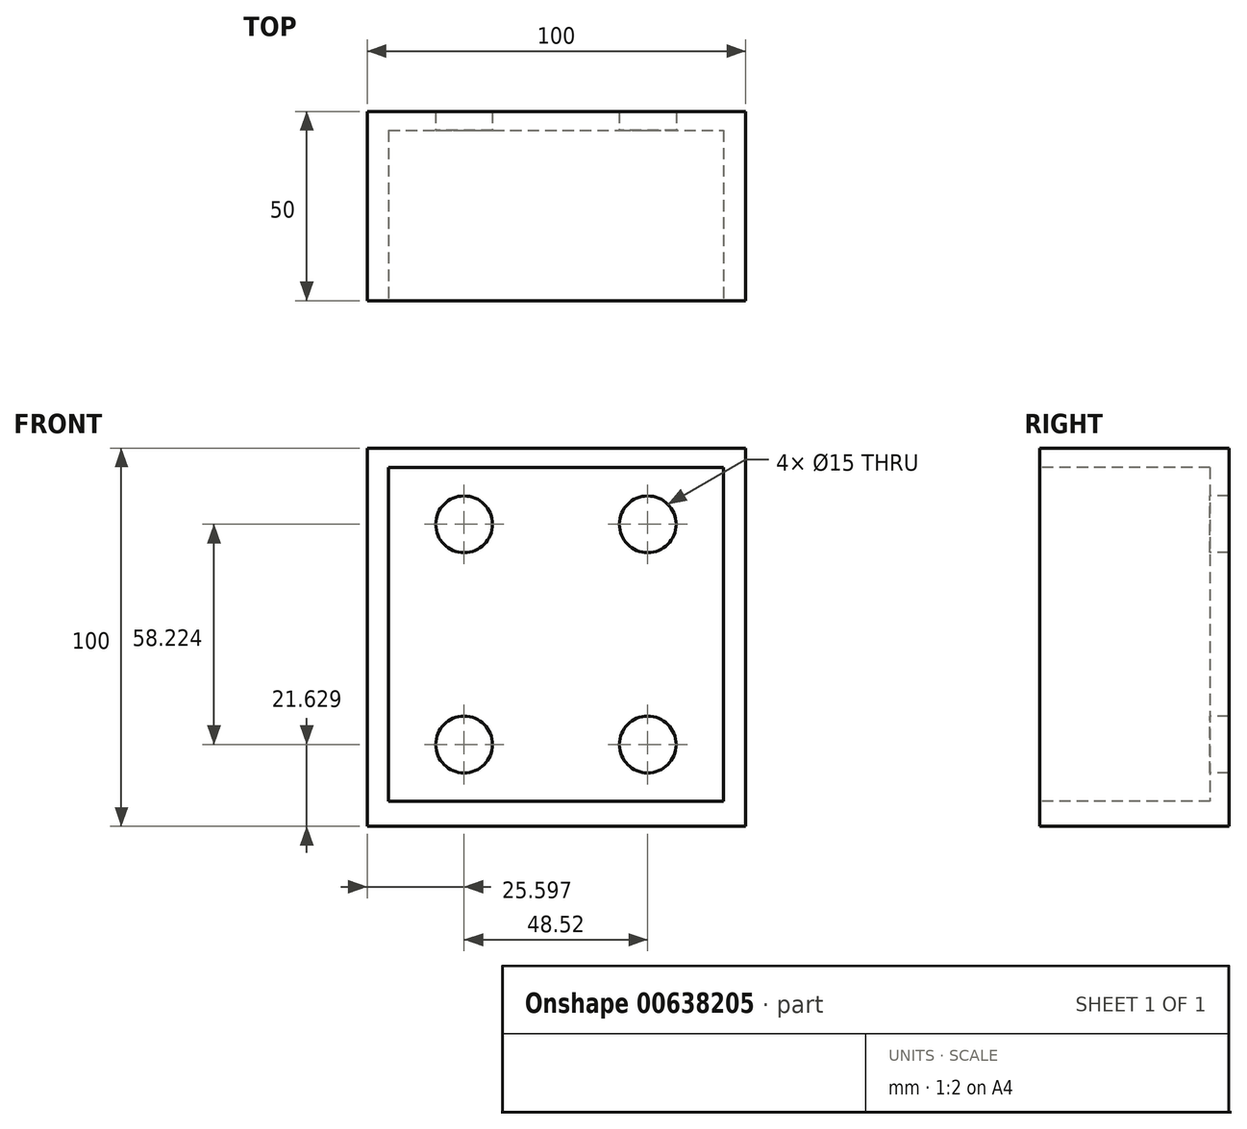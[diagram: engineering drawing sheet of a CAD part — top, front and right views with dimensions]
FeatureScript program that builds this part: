
annotation { "Feature Type Name" : "Feature", "Feature Type Description" : "" }
export const myFeature = defineFeature(function(context is Context, id is Id, definition is map)
    precondition{}
    {
        {
            var Q0;
            Q0=qCreatedBy(makeId("Front.planeOp"),FACE);
            var sketch = newSketch(context, id + "F0", { "sketchPlane" : qUnion([Q0])});
            skLineSegment(sketch, "E0.bottom", {"start": v(-46.6, 44.67) * mm, "end": v(53.4, 44.67) * mm});
            skLineSegment(sketch, "E0.top", {"start": v(-46.6, -55.33) * mm, "end": v(53.4, -55.33) * mm});
            skLineSegment(sketch, "E0.left", {"start": v(-46.6, 44.67) * mm, "end": v(-46.6, -55.33) * mm});
            skLineSegment(sketch, "E0.right", {"start": v(53.4, 44.67) * mm, "end": v(53.4, -55.33) * mm});
            skSolve(sketch);
        }
        {
            var Q0;
            Q0=makeQuery(id+"F0.imprint","IMPRINT",FACE,{"disambiguationData":[TD([[makeQuery(id+"F0.imprint","IMPRINT",EDGE,{"derivedFrom":sQuery(id+"F0.wireOp",EDGE,"E0.bottom")}),-1.0]])]});
            extrude(context, id + "F1", {"entities" : qUnion([Q0]), "depth" : 50 * mm, "offsetDistance" : 25 * mm});
        }
        {
            var Q0;
            Q0=makeQuery(id+"F1.opExtrude","CAP_FACE",FACE,{"disambiguationData":[OSD([sQuery(id+"F0.wireOp",EDGE,"E0.bottom"),sQuery(id+"F0.wireOp",EDGE,"E0.top"),sQuery(id+"F0.wireOp",EDGE,"E0.left"),sQuery(id+"F0.wireOp",EDGE,"E0.right")])],"isStart":false});
            var sketch = newSketch(context, id + "F2", { "sketchPlane" : qUnion([Q0])});
            skLineSegment(sketch, "E1.bottom", {"start": v(-41, 39.52) * mm, "end": v(47.52, 39.52) * mm});
            skLineSegment(sketch, "E1.top", {"start": v(-41, -48.7) * mm, "end": v(47.52, -48.7) * mm});
            skLineSegment(sketch, "E1.left", {"start": v(-41, 39.52) * mm, "end": v(-41, -48.7) * mm});
            skLineSegment(sketch, "E1.right", {"start": v(47.52, 39.52) * mm, "end": v(47.52, -48.7) * mm});
            skSolve(sketch);
        }
        {
            var Q0;
            Q0=makeQuery(id+"F2.imprint","IMPRINT",FACE,{"disambiguationData":[TD([[makeQuery(id+"F2.imprint","IMPRINT",EDGE,{"derivedFrom":sQuery(id+"F2.wireOp",EDGE,"E1.bottom")}),-1.0]])]});
            extrude(context, id + "F3", {"entities" : qUnion([Q0]), "operationType" : NewBodyOperationType.REMOVE, "oppositeDirection" : true, "depth" : 45 * mm, "offsetDistance" : 25 * mm});
        }
        {
            var Q0;
            Q0=makeQuery(id+"F3.boolean.opBoolean","COPY",FACE,{"derivedFrom":makeQuery(id+"F3.opExtrude","CAP_FACE",FACE,{"disambiguationData":[OSD([sQuery(id+"F2.wireOp",EDGE,"E1.bottom"),sQuery(id+"F2.wireOp",EDGE,"E1.top"),sQuery(id+"F2.wireOp",EDGE,"E1.left"),sQuery(id+"F2.wireOp",EDGE,"E1.right")])],"isStart":false})});
            var sketch = newSketch(context, id + "F4", { "sketchPlane" : qUnion([Q0])});
            skCircle(sketch, "E2", {"center": v(-21, 24.52) * mm, "radius": 7.5 * mm});
            skCircle(sketch, "E3", {"center": v(27.52, 24.52) * mm, "radius": 7.5 * mm});
            skCircle(sketch, "E4", {"center": v(-21, -33.7) * mm, "radius": 7.5 * mm});
            skCircle(sketch, "E5", {"center": v(27.52, -33.7) * mm, "radius": 7.5 * mm});
            skSolve(sketch);
        }
        {
            var Q0;
            Q0=makeQuery(id+"F4.imprint","IMPRINT",FACE,{"disambiguationData":[TD([[makeQuery(id+"F4.imprint","IMPRINT",EDGE,{"derivedFrom":sQuery(id+"F4.wireOp",EDGE,"E2")}),1.0]])]});
            var Q1;
            Q1=makeQuery(id+"F4.imprint","IMPRINT",FACE,{"disambiguationData":[TD([[makeQuery(id+"F4.imprint","IMPRINT",EDGE,{"derivedFrom":sQuery(id+"F4.wireOp",EDGE,"E3")}),1.0]])]});
            var Q2;
            Q2=makeQuery(id+"F4.imprint","IMPRINT",FACE,{"disambiguationData":[TD([[makeQuery(id+"F4.imprint","IMPRINT",EDGE,{"derivedFrom":sQuery(id+"F4.wireOp",EDGE,"E5")}),1.0]])]});
            var Q3;
            Q3=makeQuery(id+"F4.imprint","IMPRINT",FACE,{"disambiguationData":[TD([[makeQuery(id+"F4.imprint","IMPRINT",EDGE,{"derivedFrom":sQuery(id+"F4.wireOp",EDGE,"E4")}),1.0]])]});
            extrude(context, id + "F5", {"entities" : qUnion([Q0, Q1, Q2, Q3]), "operationType" : NewBodyOperationType.REMOVE, "oppositeDirection" : true, "depth" : 25 * mm, "offsetDistance" : 25 * mm});
        }
    });
